# Revit family: 879-100X0X-001-DN50-300
name_source: partatom
category: Pipe Accessories
units: mm (PartAtom-declared; Revit-internal decimal feet)

## family parameters
Always vertical = Yes
Cut with Voids When Loaded = No
Part Type = Valve - Breaks Into
Round Connector Dimension = Use Diameter
Shared = No
Work Plane-Based = No

## types (22) — shared parameters
1 = 1 mm  [stored 0.00328084 ft]
879-0050-10-144000505E4 = DN50_PN10/16
879-0050-10-144000505E7 = DN50_PN10/16
879-0065-10-144000505E4 = DN65_PN10/16
879-0065-10-144000505E7 = DN65_PN10/16
879-0080-10-144000505E4 = DN80_PN10/16
879-0080-10-144000505E7 = DN80_PN10/16
879-0100-10-144000505E4 = DN100_PN10/16
879-0100-10-144000505E7 = DN100_PN10/16
879-0150-10-144000505E4 = DN150_PN10/16
879-0150-10-144000505E7 = DN150_PN10/16
879-0200-10-044000505E4 = DN200_PN10
879-0200-10-044000505E7 = DN200_PN10
879-0200-10-144000505E4 = DN200_PN16
879-0200-10-144000505E7 = DN200_PN16
879-0250-10-044000505E4 = DN250_PN10
879-0250-10-044000505E7 = DN250_PN10
879-0250-10-144000505E4 = DN250_PN16
879-0250-10-144000505E7 = DN250_PN16
879-0300-10-044000505E4 = DN300_PN10
879-0300-10-044000505E7 = DN300_PN10
879-0300-10-144000505E4 = DN300_PN16
879-0300-10-144000505E7 = DN300_PN16
Body_wall_thickness = 10 mm  [stored 0.0328084 ft]
Description_ = AVK PRESS. RED./PRESS. RED. CONTROL VALVE
PG_Dia = 60 mm
Search_Table = 879-100X0X-001-DN50-300
URL product pages = https://www.avkvalves.com

## per-type parameters (varying)
- 879-0050-10-144000505E4_DN50_PN10/16: Body_Collar_Dia=24 mm  [stored 0.0787402 ft]; Body_Collar_Dia_2=16 mm  [stored 0.0524934 ft]; Body_Flange_Dia=66 mm; Body_Flange_Dia_2=72 mm; Body_Height_1=58 mm; Body_Height_2=29 mm; Body_Height_3=45 mm; Body_Height_4=44 mm; Body_Top_Dia=9 mm  [stored 0.0295276 ft]; Body_Top_Dia_2=8 mm  [stored 0.0262467 ft]; Body_With_Dia=29 mm; Body_With_Dia_1=58 mm; Body_With_Dia_2=58 mm; Bolt_support=121 mm; Bolt_support_2=61 mm; Bolt_support_Dia=18 mm  [stored 0.0590551 ft]; Bolt_support_Dia_ref=12 mm  [stored 0.0393701 ft]; Bolt_support_lenght=45 mm; Bolt_support_lenght_2=55 mm; Bottom_profile=13 mm; D1=50 mm; D3=83 mm; D3_Ref=280 mm; DN=50 mm; Fillet_Length=6 mm  [stored 0.019685 ft]; Flange_thickness=19 mm  [stored 0.062336 ft]; H3=415 mm; ID=25 mm  [stored 0.082021 ft]; L=230 mm; L_ref=96 mm; PG_Ref=38 mm; PG_depth=8 mm  [stored 0.0262467 ft]; PG_height=244 mm; PG_height_1=214 mm; PG_ref=45 mm; PR_1=43 mm; P_lenght=25 mm  [stored 0.082021 ft]; Pilot_Dia_1=15 mm  [stored 0.0492126 ft]; Pilot_Dia_1_ref=30 mm  [stored 0.0984252 ft]; Pilot_Dia_2=23 mm; Pilot_Dia_3=10 mm  [stored 0.0328084 ft]; Pilot_Dia_4=5 mm  [stored 0.0164042 ft]; Pilot_Dia_5=3 mm  [stored 0.00984252 ft]; Pilot_top_1=239 mm; Pilot_top_ref=83 mm; Profile1_Height=100 mm; Profile1_Length=22 mm  [stored 0.0721785 ft]; Profile1_Length_2=15 mm  [stored 0.0492126 ft]; Profile_Dia=6 mm  [stored 0.019685 ft]; Profile_Dia_2=6 mm  [stored 0.019685 ft]; Profile_Dia_3=12 mm  [stored 0.0393701 ft]; Profile_Dia_Ref=3 mm  [stored 0.00984252 ft]; Profile_height ref=41 mm  [stored 0.134514 ft]; T_Height=192 mm; T_Height_2=164 mm; T_Height_Ref=59 mm; T_Height_Ref_1=27 mm; T_Height_Ref_2=32 mm  [stored 0.104987 ft]; Top_Profile=73 mm; Top_Profile_Ref=78 mm; W=400 mm; W_Ref=280 mm; W_ref_2=394 mm
- 879-0050-10-144000505E7_DN50_PN10/16: Body_Collar_Dia=24 mm  [stored 0.0787402 ft]; Body_Collar_Dia_2=16 mm  [stored 0.0524934 ft]; Body_Flange_Dia=66 mm; Body_Flange_Dia_2=72 mm; Body_Height_1=58 mm; Body_Height_2=29 mm; Body_Height_3=50 mm; Body_Height_4=44 mm; Body_Top_Dia=9 mm  [stored 0.0295276 ft]; Body_Top_Dia_2=8 mm  [stored 0.0262467 ft]; Body_With_Dia=29 mm; Body_With_Dia_1=58 mm; Body_With_Dia_2=58 mm; Bolt_support=121 mm; Bolt_support_2=61 mm; Bolt_support_Dia=18 mm  [stored 0.0590551 ft]; Bolt_support_Dia_ref=12 mm  [stored 0.0393701 ft]; Bolt_support_lenght=45 mm; Bolt_support_lenght_2=55 mm; Bottom_profile=13 mm; D1=50 mm; D3=83 mm; D3_Ref=280 mm; DN=50 mm; Fillet_Length=6 mm  [stored 0.019685 ft]; Flange_thickness=19 mm  [stored 0.062336 ft]; H3=415 mm; ID=25 mm  [stored 0.082021 ft]; L=230 mm; L_ref=96 mm; PG_Ref=38 mm; PG_depth=8 mm  [stored 0.0262467 ft]; PG_height=252 mm; PG_height_1=222 mm; PG_ref=45 mm; PR_1=41 mm  [stored 0.134514 ft]; P_lenght=25 mm  [stored 0.082021 ft]; Pilot_Dia_1=15 mm  [stored 0.0492126 ft]; Pilot_Dia_1_ref=30 mm  [stored 0.0984252 ft]; Pilot_Dia_2=23 mm; Pilot_Dia_3=10 mm  [stored 0.0328084 ft]; Pilot_Dia_4=5 mm  [stored 0.0164042 ft]; Pilot_Dia_5=3 mm  [stored 0.00984252 ft]; Pilot_top_1=242 mm; Pilot_top_ref=81 mm; Profile1_Height=110 mm; Profile1_Length=22 mm  [stored 0.0721785 ft]; Profile1_Length_2=15 mm  [stored 0.0492126 ft]; Profile_Dia=6 mm  [stored 0.019685 ft]; Profile_Dia_2=6 mm  [stored 0.019685 ft]; Profile_Dia_3=12 mm  [stored 0.0393701 ft]; Profile_Dia_Ref=3 mm  [stored 0.00984252 ft]; Profile_height ref=41 mm  [stored 0.134514 ft]; T_Height=182 mm; T_Height_2=156 mm; T_Height_Ref=56 mm; T_Height_Ref_1=26 mm; T_Height_Ref_2=30 mm  [stored 0.0984252 ft]; Top_Profile=73 mm; Top_Profile_Ref=78 mm; W=400 mm; W_Ref=280 mm; W_ref_2=394 mm
- 879-0065-10-144000505E4_DN65_PN10/16: Body_Collar_Dia=30 mm  [stored 0.0984252 ft]; Body_Collar_Dia_2=21 mm; Body_Flange_Dia=83 mm; Body_Flange_Dia_2=91 mm; Body_Height_1=73 mm; Body_Height_2=36 mm; Body_Height_3=58 mm; Body_Height_4=51 mm; Body_Top_Dia=12 mm  [stored 0.0393701 ft]; Body_Top_Dia_2=10 mm  [stored 0.0328084 ft]; Body_With_Dia=36 mm; Body_With_Dia_1=73 mm; Body_With_Dia_2=73 mm; Bolt_support=153 mm; Bolt_support_2=76 mm; Bolt_support_Dia=18 mm  [stored 0.0590551 ft]; Bolt_support_Dia_ref=12 mm  [stored 0.0393701 ft]; Bolt_support_lenght=53 mm; Bolt_support_lenght_2=63 mm; Bottom_profile=16 mm  [stored 0.0524934 ft]; D1=59 mm; D3=93 mm; D3_Ref=305 mm; DN=65 mm; Fillet_Length=6 mm  [stored 0.019685 ft]; Flange_thickness=19 mm  [stored 0.062336 ft]; H3=445 mm; ID=33 mm  [stored 0.108268 ft]; L=290 mm; L_ref=126 mm; PG_Ref=48 mm; PG_depth=8 mm  [stored 0.0262467 ft]; PG_height=262 mm; PG_height_1=232 mm; PG_ref=53 mm; PR_1=44 mm; P_lenght=29 mm; Pilot_Dia_1=18 mm  [stored 0.0590551 ft]; Pilot_Dia_1_ref=35 mm  [stored 0.114829 ft]; Pilot_Dia_2=26 mm; Pilot_Dia_3=12 mm  [stored 0.0393701 ft]; Pilot_Dia_4=6 mm  [stored 0.019685 ft]; Pilot_Dia_5=4 mm  [stored 0.0131234 ft]; Pilot_top_1=267 mm; Pilot_top_ref=75 mm; Profile1_Height=117 mm; Profile1_Length=25 mm  [stored 0.082021 ft]; Profile1_Length_2=17 mm; Profile_Dia=6 mm  [stored 0.019685 ft]; Profile_Dia_2=6 mm  [stored 0.019685 ft]; Profile_Dia_3=12 mm  [stored 0.0393701 ft]; Profile_Dia_Ref=3 mm  [stored 0.00984252 ft]; Profile_height ref=41 mm  [stored 0.134514 ft]; T_Height=195 mm; T_Height_2=167 mm; T_Height_Ref=60 mm; T_Height_Ref_1=28 mm; T_Height_Ref_2=32 mm  [stored 0.104987 ft]; Top_Profile=92 mm; Top_Profile_Ref=97 mm; W=430 mm; W_Ref=305 mm; W_ref_2=424 mm
- 879-0065-10-144000505E7_DN65_PN10/16: Body_Collar_Dia=30 mm  [stored 0.0984252 ft]; Body_Collar_Dia_2=21 mm; Body_Flange_Dia=83 mm; Body_Flange_Dia_2=91 mm; Body_Height_1=73 mm; Body_Height_2=36 mm; Body_Height_3=73 mm; Body_Height_4=51 mm; Body_Top_Dia=12 mm  [stored 0.0393701 ft]; Body_Top_Dia_2=10 mm  [stored 0.0328084 ft]; Body_With_Dia=36 mm; Body_With_Dia_1=73 mm; Body_With_Dia_2=73 mm; Bolt_support=153 mm; Bolt_support_2=76 mm; Bolt_support_Dia=18 mm  [stored 0.0590551 ft]; Bolt_support_Dia_ref=12 mm  [stored 0.0393701 ft]; Bolt_support_lenght=53 mm; Bolt_support_lenght_2=63 mm; Bottom_profile=16 mm  [stored 0.0524934 ft]; D1=59 mm; D3=93 mm; D3_Ref=305 mm; DN=65 mm; Fillet_Length=6 mm  [stored 0.019685 ft]; Flange_thickness=19 mm  [stored 0.062336 ft]; H3=445 mm; ID=33 mm  [stored 0.108268 ft]; L=290 mm; L_ref=126 mm; PG_Ref=48 mm; PG_depth=8 mm  [stored 0.0262467 ft]; PG_height=276 mm; PG_height_1=246 mm; PG_ref=53 mm; PR_1=40 mm  [stored 0.131234 ft]; P_lenght=29 mm; Pilot_Dia_1=18 mm  [stored 0.0590551 ft]; Pilot_Dia_1_ref=35 mm  [stored 0.114829 ft]; Pilot_Dia_2=26 mm; Pilot_Dia_3=12 mm  [stored 0.0393701 ft]; Pilot_Dia_4=6 mm  [stored 0.019685 ft]; Pilot_Dia_5=4 mm  [stored 0.0131234 ft]; Pilot_top_1=274 mm; Pilot_top_ref=68 mm; Profile1_Height=135 mm; Profile1_Length=25 mm  [stored 0.082021 ft]; Profile1_Length_2=17 mm; Profile_Dia=6 mm  [stored 0.019685 ft]; Profile_Dia_2=6 mm  [stored 0.019685 ft]; Profile_Dia_3=12 mm  [stored 0.0393701 ft]; Profile_Dia_Ref=3 mm  [stored 0.00984252 ft]; Profile_height ref=41 mm  [stored 0.134514 ft]; T_Height=177 mm; T_Height_2=151 mm; T_Height_Ref=55 mm; T_Height_Ref_1=25 mm  [stored 0.082021 ft]; T_Height_Ref_2=29 mm; Top_Profile=92 mm; Top_Profile_Ref=97 mm; W=430 mm; W_Ref=305 mm; W_ref_2=424 mm
- 879-0080-10-144000505E4_DN80_PN10/16: Body_Collar_Dia=32 mm  [stored 0.104987 ft]; Body_Collar_Dia_2=22 mm  [stored 0.0721785 ft]; Body_Flange_Dia=89 mm; Body_Flange_Dia_2=97 mm; Body_Height_1=78 mm; Body_Height_2=39 mm  [stored 0.127953 ft]; Body_Height_3=62 mm; Body_Height_4=54 mm; Body_Top_Dia=12 mm  [stored 0.0393701 ft]; Body_Top_Dia_2=10 mm  [stored 0.0328084 ft]; Body_With_Dia=39 mm  [stored 0.127953 ft]; Body_With_Dia_1=78 mm; Body_With_Dia_2=78 mm; Bolt_support=163 mm; Bolt_support_2=82 mm; Bolt_support_Dia=18 mm  [stored 0.0590551 ft]; Bolt_support_Dia_ref=12 mm  [stored 0.0393701 ft]; Bolt_support_lenght=60 mm; Bolt_support_lenght_2=70 mm; Bottom_profile=20 mm  [stored 0.0656168 ft]; D1=66 mm; D3=100 mm; D3_Ref=322 mm; DN=80 mm; Fillet_Length=6 mm  [stored 0.019685 ft]; Flange_thickness=19 mm  [stored 0.062336 ft]; H3=460 mm; ID=40 mm  [stored 0.131234 ft]; L=310 mm; L_ref=136 mm; PG_Ref=52 mm; PG_depth=8 mm  [stored 0.0262467 ft]; PG_height=285 mm; PG_height_1=255 mm; PG_ref=60 mm; PR_1=40 mm  [stored 0.131234 ft]; P_lenght=32 mm  [stored 0.104987 ft]; Pilot_Dia_1=20 mm  [stored 0.0656168 ft]; Pilot_Dia_1_ref=39 mm  [stored 0.127953 ft]; Pilot_Dia_2=29 mm; Pilot_Dia_3=13 mm; Pilot_Dia_4=7 mm  [stored 0.0229659 ft]; Pilot_Dia_5=4 mm  [stored 0.0131234 ft]; Pilot_top_1=277 mm; Pilot_top_ref=73 mm; Profile1_Height=144 mm; Profile1_Length=27 mm; Profile1_Length_2=18 mm  [stored 0.0590551 ft]; Profile_Dia=6 mm  [stored 0.019685 ft]; Profile_Dia_2=6 mm  [stored 0.019685 ft]; Profile_Dia_3=12 mm  [stored 0.0393701 ft]; Profile_Dia_Ref=3 mm  [stored 0.00984252 ft]; Profile_height ref=41 mm  [stored 0.134514 ft]; T_Height=175 mm; T_Height_2=150 mm; T_Height_Ref=54 mm; T_Height_Ref_1=25 mm  [stored 0.082021 ft]; T_Height_Ref_2=29 mm; Top_Profile=98 mm; Top_Profile_Ref=103 mm; W=450 mm; W_Ref=322 mm; W_ref_2=444 mm
- 879-0080-10-144000505E7_DN80_PN10/16: Body_Collar_Dia=32 mm  [stored 0.104987 ft]; Body_Collar_Dia_2=22 mm  [stored 0.0721785 ft]; Body_Flange_Dia=89 mm; Body_Flange_Dia_2=97 mm; Body_Height_1=78 mm; Body_Height_2=39 mm  [stored 0.127953 ft]; Body_Height_3=78 mm; Body_Height_4=54 mm; Body_Top_Dia=12 mm  [stored 0.0393701 ft]; Body_Top_Dia_2=10 mm  [stored 0.0328084 ft]; Body_With_Dia=39 mm  [stored 0.127953 ft]; Body_With_Dia_1=78 mm; Body_With_Dia_2=78 mm; Bolt_support=163 mm; Bolt_support_2=82 mm; Bolt_support_Dia=18 mm  [stored 0.0590551 ft]; Bolt_support_Dia_ref=12 mm  [stored 0.0393701 ft]; Bolt_support_lenght=60 mm; Bolt_support_lenght_2=70 mm; Bottom_profile=20 mm  [stored 0.0656168 ft]; D1=66 mm; D3=100 mm; D3_Ref=322 mm; DN=80 mm; Fillet_Length=6 mm  [stored 0.019685 ft]; Flange_thickness=19 mm  [stored 0.062336 ft]; H3=460 mm; ID=40 mm  [stored 0.131234 ft]; L=310 mm; L_ref=136 mm; PG_Ref=52 mm; PG_depth=8 mm  [stored 0.0262467 ft]; PG_height=276 mm; PG_height_1=246 mm; PG_ref=60 mm; PR_1=42 mm; P_lenght=32 mm  [stored 0.104987 ft]; Pilot_Dia_1=20 mm  [stored 0.0656168 ft]; Pilot_Dia_1_ref=39 mm  [stored 0.127953 ft]; Pilot_Dia_2=29 mm; Pilot_Dia_3=13 mm; Pilot_Dia_4=7 mm  [stored 0.0229659 ft]; Pilot_Dia_5=4 mm  [stored 0.0131234 ft]; Pilot_top_1=284 mm; Pilot_top_ref=66 mm; Profile1_Height=133 mm; Profile1_Length=27 mm; Profile1_Length_2=18 mm  [stored 0.0590551 ft]; Profile_Dia=6 mm  [stored 0.019685 ft]; Profile_Dia_2=6 mm  [stored 0.019685 ft]; Profile_Dia_3=12 mm  [stored 0.0393701 ft]; Profile_Dia_Ref=3 mm  [stored 0.00984252 ft]; Profile_height ref=41 mm  [stored 0.134514 ft]; T_Height=186 mm; T_Height_2=159 mm; T_Height_Ref=58 mm; T_Height_Ref_1=27 mm; T_Height_Ref_2=31 mm  [stored 0.101706 ft]; Top_Profile=98 mm; Top_Profile_Ref=103 mm; W=450 mm; W_Ref=322 mm; W_ref_2=444 mm
- 879-0100-10-144000505E4_DN100_PN10/16: Body_Collar_Dia=36 mm; Body_Collar_Dia_2=25 mm  [stored 0.082021 ft]; Body_Flange_Dia=100 mm; Body_Flange_Dia_2=109 mm; Body_Height_1=88 mm; Body_Height_2=44 mm; Body_Height_3=59 mm; Body_Height_4=59 mm; Body_Top_Dia=14 mm  [stored 0.0459318 ft]; Body_Top_Dia_2=12 mm  [stored 0.0393701 ft]; Body_With_Dia=44 mm; Body_With_Dia_1=88 mm; Body_With_Dia_2=88 mm; Bolt_support=184 mm; Bolt_support_2=92 mm; Bolt_support_Dia=18 mm  [stored 0.0590551 ft]; Bolt_support_Dia_ref=12 mm  [stored 0.0393701 ft]; Bolt_support_lenght=70 mm; Bolt_support_lenght_2=80 mm; Bottom_profile=25 mm  [stored 0.082021 ft]; D1=78 mm; D3=110 mm; D3_Ref=355 mm; DN=100 mm; Fillet_Length=6 mm  [stored 0.019685 ft]; Flange_thickness=19 mm  [stored 0.062336 ft]; H3=480 mm; ID=50 mm; L=350 mm; L_ref=156 mm; PG_Ref=58 mm; PG_depth=8 mm  [stored 0.0262467 ft]; PG_height=291 mm; PG_height_1=261 mm; PG_ref=70 mm; PR_1=40 mm  [stored 0.131234 ft]; P_lenght=36 mm; Pilot_Dia_1=22 mm  [stored 0.0721785 ft]; Pilot_Dia_1_ref=44 mm; Pilot_Dia_2=33 mm  [stored 0.108268 ft]; Pilot_Dia_3=15 mm  [stored 0.0492126 ft]; Pilot_Dia_4=7 mm  [stored 0.0229659 ft]; Pilot_Dia_5=5 mm  [stored 0.0164042 ft]; Pilot_top_1=287 mm; Pilot_top_ref=73 mm; Profile1_Height=150 mm; Profile1_Length=30 mm  [stored 0.0984252 ft]; Profile1_Length_2=20 mm  [stored 0.0656168 ft]; Profile_Dia=6 mm  [stored 0.019685 ft]; Profile_Dia_2=6 mm  [stored 0.019685 ft]; Profile_Dia_3=12 mm  [stored 0.0393701 ft]; Profile_Dia_Ref=3 mm  [stored 0.00984252 ft]; Profile_height ref=41 mm  [stored 0.134514 ft]; T_Height=179 mm; T_Height_2=153 mm; T_Height_Ref=55 mm; T_Height_Ref_1=26 mm; T_Height_Ref_2=30 mm  [stored 0.0984252 ft]; Top_Profile=111 mm; Top_Profile_Ref=116 mm; W=495 mm; W_Ref=355 mm; W_ref_2=489 mm
- 879-0100-10-144000505E7_DN100_PN10/16: Body_Collar_Dia=36 mm; Body_Collar_Dia_2=25 mm  [stored 0.082021 ft]; Body_Flange_Dia=100 mm; Body_Flange_Dia_2=109 mm; Body_Height_1=88 mm; Body_Height_2=44 mm; Body_Height_3=70 mm; Body_Height_4=59 mm; Body_Top_Dia=14 mm  [stored 0.0459318 ft]; Body_Top_Dia_2=12 mm  [stored 0.0393701 ft]; Body_With_Dia=44 mm; Body_With_Dia_1=88 mm; Body_With_Dia_2=88 mm; Bolt_support=184 mm; Bolt_support_2=92 mm; Bolt_support_Dia=18 mm  [stored 0.0590551 ft]; Bolt_support_Dia_ref=12 mm  [stored 0.0393701 ft]; Bolt_support_lenght=70 mm; Bolt_support_lenght_2=80 mm; Bottom_profile=25 mm  [stored 0.082021 ft]; D1=78 mm; D3=110 mm; D3_Ref=355 mm; DN=100 mm; Fillet_Length=6 mm  [stored 0.019685 ft]; Flange_thickness=19 mm  [stored 0.062336 ft]; H3=480 mm; ID=50 mm; L=350 mm; L_ref=156 mm; PG_Ref=58 mm; PG_depth=8 mm  [stored 0.0262467 ft]; PG_height=285 mm; PG_height_1=255 mm; PG_ref=70 mm; PR_1=43 mm; P_lenght=36 mm; Pilot_Dia_1=22 mm  [stored 0.0721785 ft]; Pilot_Dia_1_ref=44 mm; Pilot_Dia_2=33 mm  [stored 0.108268 ft]; Pilot_Dia_3=15 mm  [stored 0.0492126 ft]; Pilot_Dia_4=7 mm  [stored 0.0229659 ft]; Pilot_Dia_5=5 mm  [stored 0.0164042 ft]; Pilot_top_1=293 mm; Pilot_top_ref=67 mm; Profile1_Height=141 mm; Profile1_Length=30 mm  [stored 0.0984252 ft]; Profile1_Length_2=20 mm  [stored 0.0656168 ft]; Profile_Dia=6 mm  [stored 0.019685 ft]; Profile_Dia_2=6 mm  [stored 0.019685 ft]; Profile_Dia_3=12 mm  [stored 0.0393701 ft]; Profile_Dia_Ref=3 mm  [stored 0.00984252 ft]; Profile_height ref=41 mm  [stored 0.134514 ft]; T_Height=188 mm; T_Height_2=161 mm; T_Height_Ref=58 mm; T_Height_Ref_1=27 mm; T_Height_Ref_2=31 mm  [stored 0.101706 ft]; Top_Profile=111 mm; Top_Profile_Ref=116 mm; W=495 mm; W_Ref=355 mm; W_ref_2=489 mm
- 879-0150-10-144000505E4_DN150_PN10/16: Body_Collar_Dia=50 mm; Body_Collar_Dia_2=34 mm; Body_Flange_Dia=137 mm; Body_Flange_Dia_2=150 mm; Body_Height_1=120 mm; Body_Height_2=60 mm; Body_Height_3=60 mm; Body_Height_4=75 mm; Body_Top_Dia=19 mm  [stored 0.062336 ft]; Body_Top_Dia_2=16 mm  [stored 0.0524934 ft]; Body_With_Dia=60 mm; Body_With_Dia_1=120 mm; Body_With_Dia_2=120 mm; Bolt_support=253 mm; Bolt_support_2=126 mm; Bolt_support_Dia=24 mm  [stored 0.0787402 ft]; Bolt_support_Dia_ref=16 mm  [stored 0.0524934 ft]; Bolt_support_lenght=95 mm; Bolt_support_lenght_2=105 mm; Bottom_profile=38 mm; D1=106 mm; D3=143 mm; D3_Ref=419 mm; DN=150 mm; Fillet_Length=8 mm  [stored 0.0262467 ft]; Flange_thickness=19 mm  [stored 0.062336 ft]; H3=615 mm; ID=75 mm; L=480 mm; L_ref=221 mm; PG_Ref=80 mm; PG_depth=11 mm  [stored 0.0360892 ft]; PG_height=351 mm; PG_height_1=321 mm; PG_ref=95 mm; PR_1=53 mm; P_lenght=51 mm; Pilot_Dia_1=31 mm  [stored 0.101706 ft]; Pilot_Dia_1_ref=62 mm; Pilot_Dia_2=47 mm; Pilot_Dia_3=21 mm; Pilot_Dia_4=10 mm  [stored 0.0328084 ft]; Pilot_Dia_5=7 mm  [stored 0.0229659 ft]; Pilot_top_1=364 mm; Pilot_top_ref=99 mm; Profile1_Height=195 mm; Profile1_Length=39 mm  [stored 0.127953 ft]; Profile1_Length_2=26 mm; Profile_Dia=8 mm  [stored 0.0262467 ft]; Profile_Dia_2=8 mm  [stored 0.0262467 ft]; Profile_Dia_3=16 mm  [stored 0.0524934 ft]; Profile_Dia_Ref=4 mm  [stored 0.0131234 ft]; Profile_height ref=43 mm; T_Height=235 mm; T_Height_2=201 mm; T_Height_Ref=73 mm; T_Height_Ref_1=34 mm; T_Height_Ref_2=39 mm  [stored 0.127953 ft]; Top_Profile=152 mm; Top_Profile_Ref=157 mm; W=560 mm; W_Ref=419 mm; W_ref_2=552 mm
- 879-0150-10-144000505E7_DN150_PN10/16: Body_Collar_Dia=50 mm; Body_Collar_Dia_2=34 mm; Body_Flange_Dia=137 mm; Body_Flange_Dia_2=150 mm; Body_Height_1=120 mm; Body_Height_2=60 mm; Body_Height_3=68 mm; Body_Height_4=75 mm; Body_Top_Dia=19 mm  [stored 0.062336 ft]; Body_Top_Dia_2=16 mm  [stored 0.0524934 ft]; Body_With_Dia=60 mm; Body_With_Dia_1=120 mm; Body_With_Dia_2=120 mm; Bolt_support=253 mm; Bolt_support_2=126 mm; Bolt_support_Dia=24 mm  [stored 0.0787402 ft]; Bolt_support_Dia_ref=16 mm  [stored 0.0524934 ft]; Bolt_support_lenght=95 mm; Bolt_support_lenght_2=105 mm; Bottom_profile=38 mm; D1=106 mm; D3=143 mm; D3_Ref=419 mm; DN=150 mm; Fillet_Length=8 mm  [stored 0.0262467 ft]; Flange_thickness=19 mm  [stored 0.062336 ft]; H3=615 mm; ID=75 mm; L=480 mm; L_ref=221 mm; PG_Ref=80 mm; PG_depth=11 mm  [stored 0.0360892 ft]; PG_height=351 mm; PG_height_1=321 mm; PG_ref=95 mm; PR_1=53 mm; P_lenght=51 mm; Pilot_Dia_1=31 mm  [stored 0.101706 ft]; Pilot_Dia_1_ref=62 mm; Pilot_Dia_2=47 mm; Pilot_Dia_3=21 mm; Pilot_Dia_4=10 mm  [stored 0.0328084 ft]; Pilot_Dia_5=7 mm  [stored 0.0229659 ft]; Pilot_top_1=368 mm; Pilot_top_ref=95 mm; Profile1_Height=195 mm; Profile1_Length=39 mm  [stored 0.127953 ft]; Profile1_Length_2=26 mm; Profile_Dia=8 mm  [stored 0.0262467 ft]; Profile_Dia_2=8 mm  [stored 0.0262467 ft]; Profile_Dia_3=16 mm  [stored 0.0524934 ft]; Profile_Dia_Ref=4 mm  [stored 0.0131234 ft]; Profile_height ref=43 mm; T_Height=235 mm; T_Height_2=201 mm; T_Height_Ref=73 mm; T_Height_Ref_1=34 mm; T_Height_Ref_2=39 mm  [stored 0.127953 ft]; Top_Profile=152 mm; Top_Profile_Ref=157 mm; W=560 mm; W_Ref=419 mm; W_ref_2=552 mm
- 879-0200-10-044000505E4_DN200_PN10: Body_Collar_Dia=63 mm; Body_Collar_Dia_2=43 mm; Body_Flange_Dia=171 mm; Body_Flange_Dia_2=188 mm; Body_Height_1=150 mm; Body_Height_2=75 mm; Body_Height_3=75 mm; Body_Height_4=90 mm; Body_Top_Dia=24 mm  [stored 0.0787402 ft]; Body_Top_Dia_2=20 mm  [stored 0.0656168 ft]; Body_With_Dia=75 mm; Body_With_Dia_1=150 mm; Body_With_Dia_2=150 mm; Bolt_support=316 mm; Bolt_support_2=158 mm; Bolt_support_Dia=30 mm  [stored 0.0984252 ft]; Bolt_support_Dia_ref=20 mm  [stored 0.0656168 ft]; Bolt_support_lenght=120 mm; Bolt_support_lenght_2=130 mm; Bottom_profile=50 mm; D1=133 mm; D3=170 mm; D3_Ref=495 mm; DN=200 mm; Fillet_Length=10 mm  [stored 0.0328084 ft]; Flange_thickness=20 mm  [stored 0.0656168 ft]; H3=690 mm; ID=100 mm; L=600 mm; L_ref=280 mm; PG_Ref=100 mm; PG_depth=14 mm  [stored 0.0459318 ft]; PG_height=397 mm; PG_height_1=367 mm; PG_ref=120 mm; PR_1=54 mm; P_lenght=64 mm; Pilot_Dia_1=39 mm  [stored 0.127953 ft]; Pilot_Dia_1_ref=77 mm; Pilot_Dia_2=58 mm; Pilot_Dia_3=26 mm; Pilot_Dia_4=13 mm; Pilot_Dia_5=9 mm  [stored 0.0295276 ft]; Pilot_top_1=418 mm; Pilot_top_ref=93 mm; Profile1_Height=238 mm; Profile1_Length=46 mm; Profile1_Length_2=31 mm  [stored 0.101706 ft]; Profile_Dia=10 mm  [stored 0.0328084 ft]; Profile_Dia_2=10 mm  [stored 0.0328084 ft]; Profile_Dia_3=20 mm  [stored 0.0656168 ft]; Profile_Dia_Ref=5 mm  [stored 0.0164042 ft]; Profile_height ref=45 mm; T_Height=237 mm; T_Height_2=203 mm; T_Height_Ref=73 mm; T_Height_Ref_1=34 mm; T_Height_Ref_2=40 mm  [stored 0.131234 ft]; Top_Profile=189 mm; Top_Profile_Ref=194 mm; W=660 mm; W_Ref=495 mm; W_ref_2=650 mm
- 879-0200-10-044000505E7_DN200_PN10: Body_Collar_Dia=63 mm; Body_Collar_Dia_2=43 mm; Body_Flange_Dia=171 mm; Body_Flange_Dia_2=188 mm; Body_Height_1=150 mm; Body_Height_2=75 mm; Body_Height_3=100 mm; Body_Height_4=90 mm; Body_Top_Dia=24 mm  [stored 0.0787402 ft]; Body_Top_Dia_2=20 mm  [stored 0.0656168 ft]; Body_With_Dia=75 mm; Body_With_Dia_1=150 mm; Body_With_Dia_2=150 mm; Bolt_support=316 mm; Bolt_support_2=158 mm; Bolt_support_Dia=30 mm  [stored 0.0984252 ft]; Bolt_support_Dia_ref=20 mm  [stored 0.0656168 ft]; Bolt_support_lenght=120 mm; Bolt_support_lenght_2=130 mm; Bottom_profile=50 mm; D1=133 mm; D3=170 mm; D3_Ref=495 mm; DN=200 mm; Fillet_Length=10 mm  [stored 0.0328084 ft]; Flange_thickness=20 mm  [stored 0.0656168 ft]; H3=774 mm; ID=100 mm; L=600 mm; L_ref=280 mm; PG_Ref=100 mm; PG_depth=14 mm  [stored 0.0459318 ft]; PG_height=417 mm; PG_height_1=387 mm; PG_ref=120 mm; PR_1=72 mm; P_lenght=64 mm; Pilot_Dia_1=39 mm  [stored 0.127953 ft]; Pilot_Dia_1_ref=77 mm; Pilot_Dia_2=58 mm; Pilot_Dia_3=26 mm; Pilot_Dia_4=13 mm; Pilot_Dia_5=9 mm  [stored 0.0295276 ft]; Pilot_top_1=472 mm; Pilot_top_ref=122 mm; Profile1_Height=240 mm; Profile1_Length=46 mm; Profile1_Length_2=31 mm  [stored 0.101706 ft]; Profile_Dia=10 mm  [stored 0.0328084 ft]; Profile_Dia_2=10 mm  [stored 0.0328084 ft]; Profile_Dia_3=20 mm  [stored 0.0656168 ft]; Profile_Dia_Ref=5 mm  [stored 0.0164042 ft]; Profile_height ref=45 mm; T_Height=319 mm; T_Height_2=273 mm; T_Height_Ref=99 mm; T_Height_Ref_1=46 mm; T_Height_Ref_2=53 mm; Top_Profile=189 mm; Top_Profile_Ref=194 mm; W=660 mm; W_Ref=495 mm; W_ref_2=650 mm
- 879-0200-10-144000505E4_DN200_PN16: Body_Collar_Dia=63 mm; Body_Collar_Dia_2=43 mm; Body_Flange_Dia=171 mm; Body_Flange_Dia_2=188 mm; Body_Height_1=150 mm; Body_Height_2=75 mm; Body_Height_3=75 mm; Body_Height_4=90 mm; Body_Top_Dia=24 mm  [stored 0.0787402 ft]; Body_Top_Dia_2=20 mm  [stored 0.0656168 ft]; Body_With_Dia=75 mm; Body_With_Dia_1=150 mm; Body_With_Dia_2=150 mm; Bolt_support=316 mm; Bolt_support_2=158 mm; Bolt_support_Dia=30 mm  [stored 0.0984252 ft]; Bolt_support_Dia_ref=20 mm  [stored 0.0656168 ft]; Bolt_support_lenght=120 mm; Bolt_support_lenght_2=130 mm; Bottom_profile=50 mm; D1=133 mm; D3=170 mm; D3_Ref=495 mm; DN=200 mm; Fillet_Length=10 mm  [stored 0.0328084 ft]; Flange_thickness=20 mm  [stored 0.0656168 ft]; H3=690 mm; ID=100 mm; L=600 mm; L_ref=280 mm; PG_Ref=100 mm; PG_depth=14 mm  [stored 0.0459318 ft]; PG_height=397 mm; PG_height_1=367 mm; PG_ref=120 mm; PR_1=54 mm; P_lenght=64 mm; Pilot_Dia_1=39 mm  [stored 0.127953 ft]; Pilot_Dia_1_ref=77 mm; Pilot_Dia_2=58 mm; Pilot_Dia_3=26 mm; Pilot_Dia_4=13 mm; Pilot_Dia_5=9 mm  [stored 0.0295276 ft]; Pilot_top_1=418 mm; Pilot_top_ref=93 mm; Profile1_Height=238 mm; Profile1_Length=46 mm; Profile1_Length_2=31 mm  [stored 0.101706 ft]; Profile_Dia=10 mm  [stored 0.0328084 ft]; Profile_Dia_2=10 mm  [stored 0.0328084 ft]; Profile_Dia_3=20 mm  [stored 0.0656168 ft]; Profile_Dia_Ref=5 mm  [stored 0.0164042 ft]; Profile_height ref=45 mm; T_Height=237 mm; T_Height_2=203 mm; T_Height_Ref=73 mm; T_Height_Ref_1=34 mm; T_Height_Ref_2=40 mm  [stored 0.131234 ft]; Top_Profile=189 mm; Top_Profile_Ref=194 mm; W=660 mm; W_Ref=495 mm; W_ref_2=650 mm
- 879-0200-10-144000505E7_DN200_PN16: Body_Collar_Dia=63 mm; Body_Collar_Dia_2=43 mm; Body_Flange_Dia=171 mm; Body_Flange_Dia_2=188 mm; Body_Height_1=150 mm; Body_Height_2=75 mm; Body_Height_3=86 mm; Body_Height_4=90 mm; Body_Top_Dia=24 mm  [stored 0.0787402 ft]; Body_Top_Dia_2=20 mm  [stored 0.0656168 ft]; Body_With_Dia=75 mm; Body_With_Dia_1=150 mm; Body_With_Dia_2=150 mm; Bolt_support=316 mm; Bolt_support_2=158 mm; Bolt_support_Dia=30 mm  [stored 0.0984252 ft]; Bolt_support_Dia_ref=20 mm  [stored 0.0656168 ft]; Bolt_support_lenght=120 mm; Bolt_support_lenght_2=130 mm; Bottom_profile=50 mm; D1=133 mm; D3=170 mm; D3_Ref=495 mm; DN=200 mm; Fillet_Length=10 mm  [stored 0.0328084 ft]; Flange_thickness=20 mm  [stored 0.0656168 ft]; H3=774 mm; ID=100 mm; L=600 mm; L_ref=280 mm; PG_Ref=100 mm; PG_depth=14 mm  [stored 0.0459318 ft]; PG_height=417 mm; PG_height_1=387 mm; PG_ref=120 mm; PR_1=72 mm; P_lenght=64 mm; Pilot_Dia_1=39 mm  [stored 0.127953 ft]; Pilot_Dia_1_ref=77 mm; Pilot_Dia_2=58 mm; Pilot_Dia_3=26 mm; Pilot_Dia_4=13 mm; Pilot_Dia_5=9 mm  [stored 0.0295276 ft]; Pilot_top_1=465 mm; Pilot_top_ref=129 mm; Profile1_Height=240 mm; Profile1_Length=46 mm; Profile1_Length_2=31 mm  [stored 0.101706 ft]; Profile_Dia=10 mm  [stored 0.0328084 ft]; Profile_Dia_2=10 mm  [stored 0.0328084 ft]; Profile_Dia_3=20 mm  [stored 0.0656168 ft]; Profile_Dia_Ref=5 mm  [stored 0.0164042 ft]; Profile_height ref=45 mm; T_Height=319 mm; T_Height_2=273 mm; T_Height_Ref=99 mm; T_Height_Ref_1=46 mm; T_Height_Ref_2=53 mm; Top_Profile=189 mm; Top_Profile_Ref=194 mm; W=660 mm; W_Ref=495 mm; W_ref_2=650 mm
- 879-0250-10-044000505E4_DN250_PN10: Body_Collar_Dia=76 mm; Body_Collar_Dia_2=52 mm; Body_Flange_Dia=209 mm; Body_Flange_Dia_2=228 mm; Body_Height_1=183 mm; Body_Height_2=91 mm; Body_Height_3=81 mm; Body_Height_4=106 mm; Body_Top_Dia=29 mm; Body_Top_Dia_2=24 mm  [stored 0.0787402 ft]; Body_With_Dia=91 mm; Body_With_Dia_1=183 mm; Body_With_Dia_2=183 mm; Bolt_support=384 mm; Bolt_support_2=192 mm; Bolt_support_Dia=30 mm  [stored 0.0984252 ft]; Bolt_support_Dia_ref=20 mm  [stored 0.0656168 ft]; Bolt_support_lenght=145 mm; Bolt_support_lenght_2=155 mm; Bottom_profile=63 mm; D1=160 mm; D3=198 mm; D3_Ref=523 mm; DN=250 mm; Fillet_Length=10 mm  [stored 0.0328084 ft]; Flange_thickness=22 mm  [stored 0.0721785 ft]; H3=770 mm; ID=125 mm; L=730 mm; L_ref=343 mm; PG_Ref=122 mm; PG_depth=14 mm  [stored 0.0459318 ft]; PG_height=450 mm; PG_height_1=420 mm; PG_ref=145 mm; PR_1=53 mm; P_lenght=76 mm; Pilot_Dia_1=46 mm; Pilot_Dia_1_ref=92 mm; Pilot_Dia_2=69 mm; Pilot_Dia_3=31 mm  [stored 0.101706 ft]; Pilot_Dia_4=15 mm  [stored 0.0492126 ft]; Pilot_Dia_5=10 mm  [stored 0.0328084 ft]; Pilot_top_1=471 mm; Pilot_top_ref=91 mm; Profile1_Height=292 mm; Profile1_Length=53 mm; Profile1_Length_2=36 mm; Profile_Dia=10 mm  [stored 0.0328084 ft]; Profile_Dia_2=10 mm  [stored 0.0328084 ft]; Profile_Dia_3=20 mm  [stored 0.0656168 ft]; Profile_Dia_Ref=5 mm  [stored 0.0164042 ft]; Profile_height ref=45 mm; T_Height=236 mm; T_Height_2=202 mm; T_Height_Ref=73 mm; T_Height_Ref_1=34 mm; T_Height_Ref_2=39 mm  [stored 0.127953 ft]; Top_Profile=231 mm; Top_Profile_Ref=236 mm; W=660 mm; W_Ref=523 mm; W_ref_2=650 mm
- 879-0250-10-044000505E7_DN250_PN10: Body_Collar_Dia=76 mm; Body_Collar_Dia_2=52 mm; Body_Flange_Dia=209 mm; Body_Flange_Dia_2=228 mm; Body_Height_1=183 mm; Body_Height_2=91 mm; Body_Height_3=105 mm; Body_Height_4=106 mm; Body_Top_Dia=29 mm; Body_Top_Dia_2=24 mm  [stored 0.0787402 ft]; Body_With_Dia=91 mm; Body_With_Dia_1=183 mm; Body_With_Dia_2=183 mm; Bolt_support=384 mm; Bolt_support_2=192 mm; Bolt_support_Dia=30 mm  [stored 0.0984252 ft]; Bolt_support_Dia_ref=20 mm  [stored 0.0656168 ft]; Bolt_support_lenght=145 mm; Bolt_support_lenght_2=155 mm; Bottom_profile=63 mm; D1=160 mm; D3=198 mm; D3_Ref=523 mm; DN=250 mm; Fillet_Length=10 mm  [stored 0.0328084 ft]; Flange_thickness=22 mm  [stored 0.0721785 ft]; H3=854 mm; ID=125 mm; L=730 mm; L_ref=343 mm; PG_Ref=122 mm; PG_depth=14 mm  [stored 0.0459318 ft]; PG_height=472 mm; PG_height_1=442 mm; PG_ref=145 mm; PR_1=72 mm; P_lenght=76 mm; Pilot_Dia_1=46 mm; Pilot_Dia_1_ref=92 mm; Pilot_Dia_2=69 mm; Pilot_Dia_3=31 mm  [stored 0.101706 ft]; Pilot_Dia_4=15 mm  [stored 0.0492126 ft]; Pilot_Dia_5=10 mm  [stored 0.0328084 ft]; Pilot_top_1=525 mm; Pilot_top_ref=122 mm; Profile1_Height=295 mm; Profile1_Length=53 mm; Profile1_Length_2=36 mm; Profile_Dia=10 mm  [stored 0.0328084 ft]; Profile_Dia_2=10 mm  [stored 0.0328084 ft]; Profile_Dia_3=20 mm  [stored 0.0656168 ft]; Profile_Dia_Ref=5 mm  [stored 0.0164042 ft]; Profile_height ref=45 mm; T_Height=317 mm; T_Height_2=271 mm; T_Height_Ref=98 mm; T_Height_Ref_1=45 mm; T_Height_Ref_2=53 mm; Top_Profile=231 mm; Top_Profile_Ref=236 mm; W=660 mm; W_Ref=523 mm; W_ref_2=650 mm
- 879-0250-10-144000505E4_DN250_PN16: Body_Collar_Dia=76 mm; Body_Collar_Dia_2=52 mm; Body_Flange_Dia=209 mm; Body_Flange_Dia_2=228 mm; Body_Height_1=183 mm; Body_Height_2=91 mm; Body_Height_3=81 mm; Body_Height_4=106 mm; Body_Top_Dia=29 mm; Body_Top_Dia_2=24 mm  [stored 0.0787402 ft]; Body_With_Dia=91 mm; Body_With_Dia_1=183 mm; Body_With_Dia_2=183 mm; Bolt_support=384 mm; Bolt_support_2=192 mm; Bolt_support_Dia=30 mm  [stored 0.0984252 ft]; Bolt_support_Dia_ref=20 mm  [stored 0.0656168 ft]; Bolt_support_lenght=145 mm; Bolt_support_lenght_2=155 mm; Bottom_profile=63 mm; D1=160 mm; D3=203 mm; D3_Ref=528 mm; DN=250 mm; Fillet_Length=10 mm  [stored 0.0328084 ft]; Flange_thickness=22 mm  [stored 0.0721785 ft]; H3=770 mm; ID=125 mm; L=730 mm; L_ref=343 mm; PG_Ref=122 mm; PG_depth=14 mm  [stored 0.0459318 ft]; PG_height=455 mm; PG_height_1=425 mm; PG_ref=145 mm; PR_1=50 mm; P_lenght=78 mm; Pilot_Dia_1=47 mm; Pilot_Dia_1_ref=94 mm; Pilot_Dia_2=71 mm; Pilot_Dia_3=31 mm  [stored 0.101706 ft]; Pilot_Dia_4=16 mm  [stored 0.0524934 ft]; Pilot_Dia_5=10 mm  [stored 0.0328084 ft]; Pilot_top_1=469 mm; Pilot_top_ref=89 mm; Profile1_Height=300 mm; Profile1_Length=55 mm; Profile1_Length_2=36 mm; Profile_Dia=10 mm  [stored 0.0328084 ft]; Profile_Dia_2=10 mm  [stored 0.0328084 ft]; Profile_Dia_3=20 mm  [stored 0.0656168 ft]; Profile_Dia_Ref=5 mm  [stored 0.0164042 ft]; Profile_height ref=45 mm; T_Height=223 mm; T_Height_2=191 mm; T_Height_Ref=69 mm; T_Height_Ref_1=32 mm  [stored 0.104987 ft]; T_Height_Ref_2=37 mm; Top_Profile=231 mm; Top_Profile_Ref=236 mm; W=660 mm; W_Ref=528 mm; W_ref_2=650 mm
- 879-0250-10-144000505E7_DN250_PN16: Body_Collar_Dia=76 mm; Body_Collar_Dia_2=52 mm; Body_Flange_Dia=209 mm; Body_Flange_Dia_2=228 mm; Body_Height_1=183 mm; Body_Height_2=91 mm; Body_Height_3=81 mm; Body_Height_4=106 mm; Body_Top_Dia=29 mm; Body_Top_Dia_2=24 mm  [stored 0.0787402 ft]; Body_With_Dia=91 mm; Body_With_Dia_1=183 mm; Body_With_Dia_2=183 mm; Bolt_support=384 mm; Bolt_support_2=192 mm; Bolt_support_Dia=30 mm  [stored 0.0984252 ft]; Bolt_support_Dia_ref=20 mm  [stored 0.0656168 ft]; Bolt_support_lenght=145 mm; Bolt_support_lenght_2=155 mm; Bottom_profile=63 mm; D1=160 mm; D3=203 mm; D3_Ref=528 mm; DN=250 mm; Fillet_Length=10 mm  [stored 0.0328084 ft]; Flange_thickness=22 mm  [stored 0.0721785 ft]; H3=854 mm; ID=125 mm; L=730 mm; L_ref=343 mm; PG_Ref=122 mm; PG_depth=14 mm  [stored 0.0459318 ft]; PG_height=486 mm; PG_height_1=456 mm; PG_ref=145 mm; PR_1=66 mm; P_lenght=78 mm; Pilot_Dia_1=47 mm; Pilot_Dia_1_ref=94 mm; Pilot_Dia_2=71 mm; Pilot_Dia_3=31 mm  [stored 0.101706 ft]; Pilot_Dia_4=16 mm  [stored 0.0524934 ft]; Pilot_Dia_5=10 mm  [stored 0.0328084 ft]; Pilot_top_1=511 mm; Pilot_top_ref=131 mm; Profile1_Height=315 mm; Profile1_Length=55 mm; Profile1_Length_2=36 mm; Profile_Dia=10 mm  [stored 0.0328084 ft]; Profile_Dia_2=10 mm  [stored 0.0328084 ft]; Profile_Dia_3=20 mm  [stored 0.0656168 ft]; Profile_Dia_Ref=5 mm  [stored 0.0164042 ft]; Profile_height ref=45 mm; T_Height=292 mm; T_Height_2=250 mm; T_Height_Ref=90 mm; T_Height_Ref_1=42 mm; T_Height_Ref_2=49 mm; Top_Profile=231 mm; Top_Profile_Ref=236 mm; W=660 mm; W_Ref=528 mm; W_ref_2=650 mm
- 879-0300-10-044000505E4_DN300_PN10: Body_Collar_Dia=89 mm; Body_Collar_Dia_2=61 mm; Body_Flange_Dia=243 mm; Body_Flange_Dia_2=266 mm; Body_Height_1=213 mm; Body_Height_2=106 mm; Body_Height_3=95 mm; Body_Height_4=121 mm; Body_Top_Dia=34 mm; Body_Top_Dia_2=28 mm; Body_With_Dia=106 mm; Body_With_Dia_1=213 mm; Body_With_Dia_2=213 mm; Bolt_support=447 mm; Bolt_support_2=224 mm; Bolt_support_Dia=30 mm  [stored 0.0984252 ft]; Bolt_support_Dia_ref=20 mm  [stored 0.0656168 ft]; Bolt_support_lenght=170 mm; Bolt_support_lenght_2=180 mm; Bottom_profile=75 mm; D1=185 mm; D3=223 mm; D3_Ref=570 mm; DN=300 mm; Fillet_Length=10 mm  [stored 0.0328084 ft]; Flange_thickness=25 mm  [stored 0.082021 ft]; H3=840 mm; ID=150 mm; L=850 mm; L_ref=401 mm; PG_Ref=142 mm; PG_depth=14 mm  [stored 0.0459318 ft]; PG_height=471 mm; PG_height_1=441 mm; PG_ref=170 mm; PR_1=61 mm; P_lenght=87 mm; Pilot_Dia_1=53 mm; Pilot_Dia_1_ref=105 mm; Pilot_Dia_2=79 mm; Pilot_Dia_3=35 mm  [stored 0.114829 ft]; Pilot_Dia_4=18 mm  [stored 0.0590551 ft]; Pilot_Dia_5=12 mm  [stored 0.0393701 ft]; Pilot_top_1=523 mm; Pilot_top_ref=85 mm; Profile1_Height=305 mm; Profile1_Length=60 mm; Profile1_Length_2=40 mm  [stored 0.131234 ft]; Profile_Dia=10 mm  [stored 0.0328084 ft]; Profile_Dia_2=10 mm  [stored 0.0328084 ft]; Profile_Dia_3=20 mm  [stored 0.0656168 ft]; Profile_Dia_Ref=5 mm  [stored 0.0164042 ft]; Profile_height ref=45 mm; T_Height=268 mm; T_Height_2=229 mm; T_Height_Ref=83 mm; T_Height_Ref_1=38 mm; T_Height_Ref_2=45 mm; Top_Profile=268 mm; Top_Profile_Ref=273 mm; W=705 mm; W_Ref=570 mm; W_ref_2=695 mm
- 879-0300-10-044000505E7_DN300_PN10: Body_Collar_Dia=89 mm; Body_Collar_Dia_2=61 mm; Body_Flange_Dia=243 mm; Body_Flange_Dia_2=266 mm; Body_Height_1=213 mm; Body_Height_2=106 mm; Body_Height_3=106 mm; Body_Height_4=121 mm; Body_Top_Dia=34 mm; Body_Top_Dia_2=28 mm; Body_With_Dia=106 mm; Body_With_Dia_1=213 mm; Body_With_Dia_2=213 mm; Bolt_support=447 mm; Bolt_support_2=224 mm; Bolt_support_Dia=30 mm  [stored 0.0984252 ft]; Bolt_support_Dia_ref=20 mm  [stored 0.0656168 ft]; Bolt_support_lenght=170 mm; Bolt_support_lenght_2=180 mm; Bottom_profile=75 mm; D1=185 mm; D3=223 mm; D3_Ref=570 mm; DN=300 mm; Fillet_Length=10 mm  [stored 0.0328084 ft]; Flange_thickness=25 mm  [stored 0.082021 ft]; H3=923 mm; ID=150 mm; L=850 mm; L_ref=401 mm; PG_Ref=142 mm; PG_depth=14 mm  [stored 0.0459318 ft]; PG_height=512 mm; PG_height_1=482 mm; PG_ref=170 mm; PR_1=72 mm; P_lenght=87 mm; Pilot_Dia_1=53 mm; Pilot_Dia_1_ref=105 mm; Pilot_Dia_2=79 mm; Pilot_Dia_3=35 mm  [stored 0.114829 ft]; Pilot_Dia_4=18 mm  [stored 0.0590551 ft]; Pilot_Dia_5=12 mm  [stored 0.0393701 ft]; Pilot_top_1=570 mm; Pilot_top_ref=120 mm; Profile1_Height=335 mm; Profile1_Length=60 mm; Profile1_Length_2=40 mm  [stored 0.131234 ft]; Profile_Dia=10 mm  [stored 0.0328084 ft]; Profile_Dia_2=10 mm  [stored 0.0328084 ft]; Profile_Dia_3=20 mm  [stored 0.0656168 ft]; Profile_Dia_Ref=5 mm  [stored 0.0164042 ft]; Profile_height ref=45 mm; T_Height=321 mm; T_Height_2=275 mm; T_Height_Ref=99 mm; T_Height_Ref_1=46 mm; T_Height_Ref_2=53 mm; Top_Profile=268 mm; Top_Profile_Ref=273 mm; W=705 mm; W_Ref=570 mm; W_ref_2=695 mm
- 879-0300-10-144000505E4_DN300_PN16: Body_Collar_Dia=89 mm; Body_Collar_Dia_2=61 mm; Body_Flange_Dia=243 mm; Body_Flange_Dia_2=266 mm; Body_Height_1=213 mm; Body_Height_2=106 mm; Body_Height_3=95 mm; Body_Height_4=121 mm; Body_Top_Dia=34 mm; Body_Top_Dia_2=28 mm; Body_With_Dia=106 mm; Body_With_Dia_1=213 mm; Body_With_Dia_2=213 mm; Bolt_support=447 mm; Bolt_support_2=224 mm; Bolt_support_Dia=30 mm  [stored 0.0984252 ft]; Bolt_support_Dia_ref=20 mm  [stored 0.0656168 ft]; Bolt_support_lenght=170 mm; Bolt_support_lenght_2=180 mm; Bottom_profile=75 mm; D1=185 mm; D3=230 mm; D3_Ref=578 mm; DN=300 mm; Fillet_Length=10 mm  [stored 0.0328084 ft]; Flange_thickness=25 mm  [stored 0.082021 ft]; H3=840 mm; ID=150 mm; L=850 mm; L_ref=401 mm; PG_Ref=142 mm; PG_depth=14 mm  [stored 0.0459318 ft]; PG_height=469 mm; PG_height_1=439 mm; PG_ref=170 mm; PR_1=59 mm; P_lenght=90 mm; Pilot_Dia_1=55 mm; Pilot_Dia_1_ref=109 mm; Pilot_Dia_2=82 mm; Pilot_Dia_3=36 mm; Pilot_Dia_4=18 mm  [stored 0.0590551 ft]; Pilot_Dia_5=12 mm  [stored 0.0393701 ft]; Pilot_top_1=519 mm; Pilot_top_ref=81 mm; Profile1_Height=305 mm; Profile1_Length=62 mm; Profile1_Length_2=41 mm  [stored 0.134514 ft]; Profile_Dia=10 mm  [stored 0.0328084 ft]; Profile_Dia_2=10 mm  [stored 0.0328084 ft]; Profile_Dia_3=20 mm  [stored 0.0656168 ft]; Profile_Dia_Ref=5 mm  [stored 0.0164042 ft]; Profile_height ref=45 mm; T_Height=260 mm; T_Height_2=223 mm; T_Height_Ref=80 mm; T_Height_Ref_1=37 mm; T_Height_Ref_2=43 mm; Top_Profile=268 mm; Top_Profile_Ref=273 mm; W=705 mm; W_Ref=578 mm; W_ref_2=695 mm
- 879-0300-10-144000505E7_DN300_PN16: Body_Collar_Dia=89 mm; Body_Collar_Dia_2=61 mm; Body_Flange_Dia=243 mm; Body_Flange_Dia_2=266 mm; Body_Height_1=213 mm; Body_Height_2=106 mm; Body_Height_3=95 mm; Body_Height_4=121 mm; Body_Top_Dia=34 mm; Body_Top_Dia_2=28 mm; Body_With_Dia=106 mm; Body_With_Dia_1=213 mm; Body_With_Dia_2=213 mm; Bolt_support=447 mm; Bolt_support_2=224 mm; Bolt_support_Dia=30 mm  [stored 0.0984252 ft]; Bolt_support_Dia_ref=20 mm  [stored 0.0656168 ft]; Bolt_support_lenght=170 mm; Bolt_support_lenght_2=180 mm; Bottom_profile=75 mm; D1=185 mm; D3=230 mm; D3_Ref=578 mm; DN=300 mm; Fillet_Length=10 mm  [stored 0.0328084 ft]; Flange_thickness=25 mm  [stored 0.082021 ft]; H3=923 mm; ID=150 mm; L=850 mm; L_ref=401 mm; PG_Ref=142 mm; PG_depth=14 mm  [stored 0.0459318 ft]; PG_height=503 mm; PG_height_1=473 mm; PG_ref=170 mm; PR_1=73 mm; P_lenght=90 mm; Pilot_Dia_1=55 mm; Pilot_Dia_1_ref=109 mm; Pilot_Dia_2=82 mm; Pilot_Dia_3=36 mm; Pilot_Dia_4=18 mm  [stored 0.0590551 ft]; Pilot_Dia_5=12 mm  [stored 0.0393701 ft]; Pilot_top_1=561 mm; Pilot_top_ref=122 mm; Profile1_Height=325 mm; Profile1_Length=62 mm; Profile1_Length_2=41 mm  [stored 0.134514 ft]; Profile_Dia=10 mm  [stored 0.0328084 ft]; Profile_Dia_2=10 mm  [stored 0.0328084 ft]; Profile_Dia_3=20 mm  [stored 0.0656168 ft]; Profile_Dia_Ref=5 mm  [stored 0.0164042 ft]; Profile_height ref=45 mm; T_Height=323 mm; T_Height_2=277 mm; T_Height_Ref=100 mm; T_Height_Ref_1=46 mm; T_Height_Ref_2=54 mm; Top_Profile=268 mm; Top_Profile_Ref=273 mm; W=705 mm; W_Ref=578 mm; W_ref_2=695 mm

note: [stored X ft] marks values corroborated as IEEE doubles in the binary element streams (Revit-internal decimal feet)

## geometry (parser evidence)
native form markers: Sweep x3
no freeform markers — native parametric forms only
